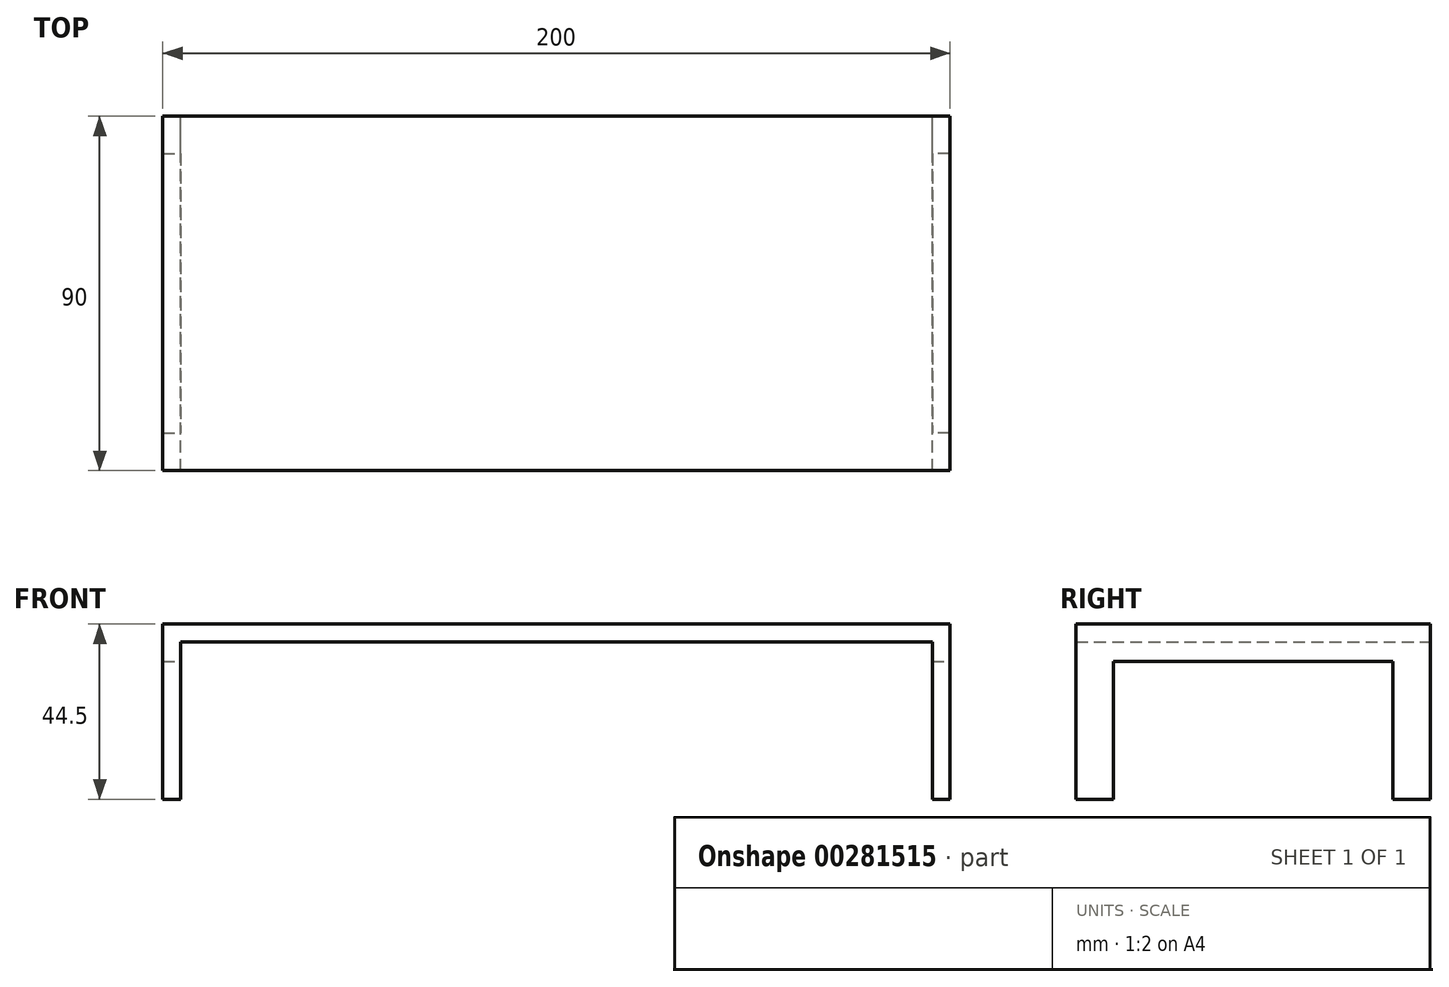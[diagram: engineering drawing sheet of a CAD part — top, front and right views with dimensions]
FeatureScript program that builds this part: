
annotation { "Feature Type Name" : "Feature", "Feature Type Description" : "" }
export const myFeature = defineFeature(function(context is Context, id is Id, definition is map)
    precondition{}
    {
        {
            var Q0;
            Q0=qCreatedBy(makeId("Front.planeOp"),FACE);
            var sketch = newSketch(context, id + "F0", { "sketchPlane" : qUnion([Q0])});
            skLineSegment(sketch, "E0.bottom", {"start": v(-100, 0) * mm, "end": v(-95.5, 0) * mm});
            skLineSegment(sketch, "E0.top", {"start": v(-100, 40) * mm, "end": v(-95.5, 40) * mm});
            skLineSegment(sketch, "E0.left", {"start": v(-100, 0) * mm, "end": v(-100, 40) * mm});
            skLineSegment(sketch, "E0.right", {"start": v(-95.5, 0) * mm, "end": v(-95.5, 40) * mm});
            skLineSegment(sketch, "E1.MirrorCS", {"start": v(95.5, 0) * mm, "end": v(95.5, 40) * mm});
            skLineSegment(sketch, "E2.MirrorCS", {"start": v(100, 0) * mm, "end": v(100, 40) * mm});
            skLineSegment(sketch, "E3.MirrorCS", {"start": v(100, 0) * mm, "end": v(95.5, 0) * mm});
            skLineSegment(sketch, "E4.MirrorCS", {"start": v(100, 40) * mm, "end": v(95.5, 40) * mm});
            skLineSegment(sketch, "E5.bottom", {"start": v(-100, 40) * mm, "end": v(100, 40) * mm});
            skLineSegment(sketch, "E5.top", {"start": v(-100, 44.5) * mm, "end": v(100, 44.5) * mm});
            skLineSegment(sketch, "E5.left", {"start": v(-100, 40) * mm, "end": v(-100, 44.5) * mm});
            skLineSegment(sketch, "E5.right", {"start": v(100, 40) * mm, "end": v(100, 44.5) * mm});
            skLineSegment(sketch, "E6.bottom", {"start": v(-85.5, 0) * mm, "end": v(-95, 0) * mm});
            skLineSegment(sketch, "E6.top", {"start": v(-85.5, 35) * mm, "end": v(-95, 35) * mm});
            skLineSegment(sketch, "E6.left", {"start": v(-85.5, 0) * mm, "end": v(-85.5, 35) * mm});
            skLineSegment(sketch, "E6.right", {"start": v(-95, 0) * mm, "end": v(-95, 35) * mm});
            skLineSegment(sketch, "E7.MirrorCS", {"start": v(85.5, 0) * mm, "end": v(95, 0) * mm});
            skLineSegment(sketch, "E8.MirrorCS", {"start": v(85.5, 0) * mm, "end": v(85.5, 35) * mm});
            skLineSegment(sketch, "E9.MirrorCS", {"start": v(85.5, 35) * mm, "end": v(95, 35) * mm});
            skLineSegment(sketch, "E10.MirrorCS", {"start": v(95, 0) * mm, "end": v(95, 35) * mm});
            skLineSegment(sketch, "E11.bottom", {"start": v(-95, 35) * mm, "end": v(95, 35) * mm});
            skLineSegment(sketch, "E11.top", {"start": v(-95, 39.5) * mm, "end": v(95, 39.5) * mm});
            skLineSegment(sketch, "E11.left", {"start": v(-95, 35) * mm, "end": v(-95, 39.5) * mm});
            skLineSegment(sketch, "E11.right", {"start": v(95, 35) * mm, "end": v(95, 39.5) * mm});
            skSolve(sketch);
        }
        {
            var Q0;
            Q0=makeQuery(id+"F0.imprint","IMPRINT",FACE,{"disambiguationData":[TD([[makeQuery(id+"F0.imprint","IMPRINT",EDGE,{"derivedFrom":sQuery(id+"F0.wireOp",EDGE,"E5.top")}),-1.0]])]});
            var Q1;
            Q1=makeQuery(id+"F0.imprint","IMPRINT",FACE,{"disambiguationData":[TD([[makeQuery(id+"F0.imprint","IMPRINT",EDGE,{"derivedFrom":sQuery(id+"F0.wireOp",EDGE,"E0.bottom")}),1.0]])]});
            var Q2;
            {var subQ0=sQuery(id+"F0.wireOp",EDGE,"E1.MirrorCS");Q2=makeQuery(id+"F0.imprint","IMPRINT",FACE,{"disambiguationData":[TD([[makeQuery(id+"F0.imprint","IMPRINT",EDGE,{"derivedFrom":subQ0}),-1.0]])]});}
            extrude(context, id + "F1", {"entities" : qUnion([Q0, Q1, Q2]), "depth" : 90 * mm});
        }
        {
            var Q0;
            Q0=makeQuery(id+"F1.opExtrude","SWEPT_FACE",FACE,{"disambiguationData":[OSD([sQuery(id+"F0.wireOp",EDGE,"E2.MirrorCS"),sQuery(id+"F0.wireOp",EDGE,"E5.right")])]});
            var sketch = newSketch(context, id + "F2", { "sketchPlane" : qUnion([Q0])});
            skLineSegment(sketch, "E12.bottom", {"start": v(-80.5, 35) * mm, "end": v(-9.5, 35) * mm});
            skLineSegment(sketch, "E12.top", {"start": v(-80.5, -35) * mm, "end": v(-9.5, -35) * mm});
            skLineSegment(sketch, "E12.left", {"start": v(-80.5, 35) * mm, "end": v(-80.5, -35) * mm});
            skLineSegment(sketch, "E12.right", {"start": v(-9.5, 35) * mm, "end": v(-9.5, -35) * mm});
            skPoint(sketch, "E12.middle", {"position": v(-45, 0) * mm});
            skSolve(sketch);
        }
        {
            var Q0;
            {var subQ0=sQuery(id+"F2.wireOp",EDGE,"E12.bottom");Q0=makeQuery(id+"F2.imprint","IMPRINT",FACE,{"disambiguationData":[TD([[makeQuery(id+"F2.imprint","IMPRINT",EDGE,{"derivedFrom":subQ0}),-1.0]])]});}
            var Q1;
            {var subQ0=sQuery(id+"F2.wireOp",EDGE,"E12.top");Q1=makeQuery(id+"F2.imprint","IMPRINT",FACE,{"disambiguationData":[TD([[makeQuery(id+"F2.imprint","IMPRINT",EDGE,{"derivedFrom":subQ0}),1.0]])]});}
            extrude(context, id + "F3", {"entities" : qUnion([Q0, Q1]), "operationType" : NewBodyOperationType.REMOVE, "endBound" : BoundingType.THROUGH_ALL, "oppositeDirection" : true, "depth" : 151.8 * mm});
        }
    });
